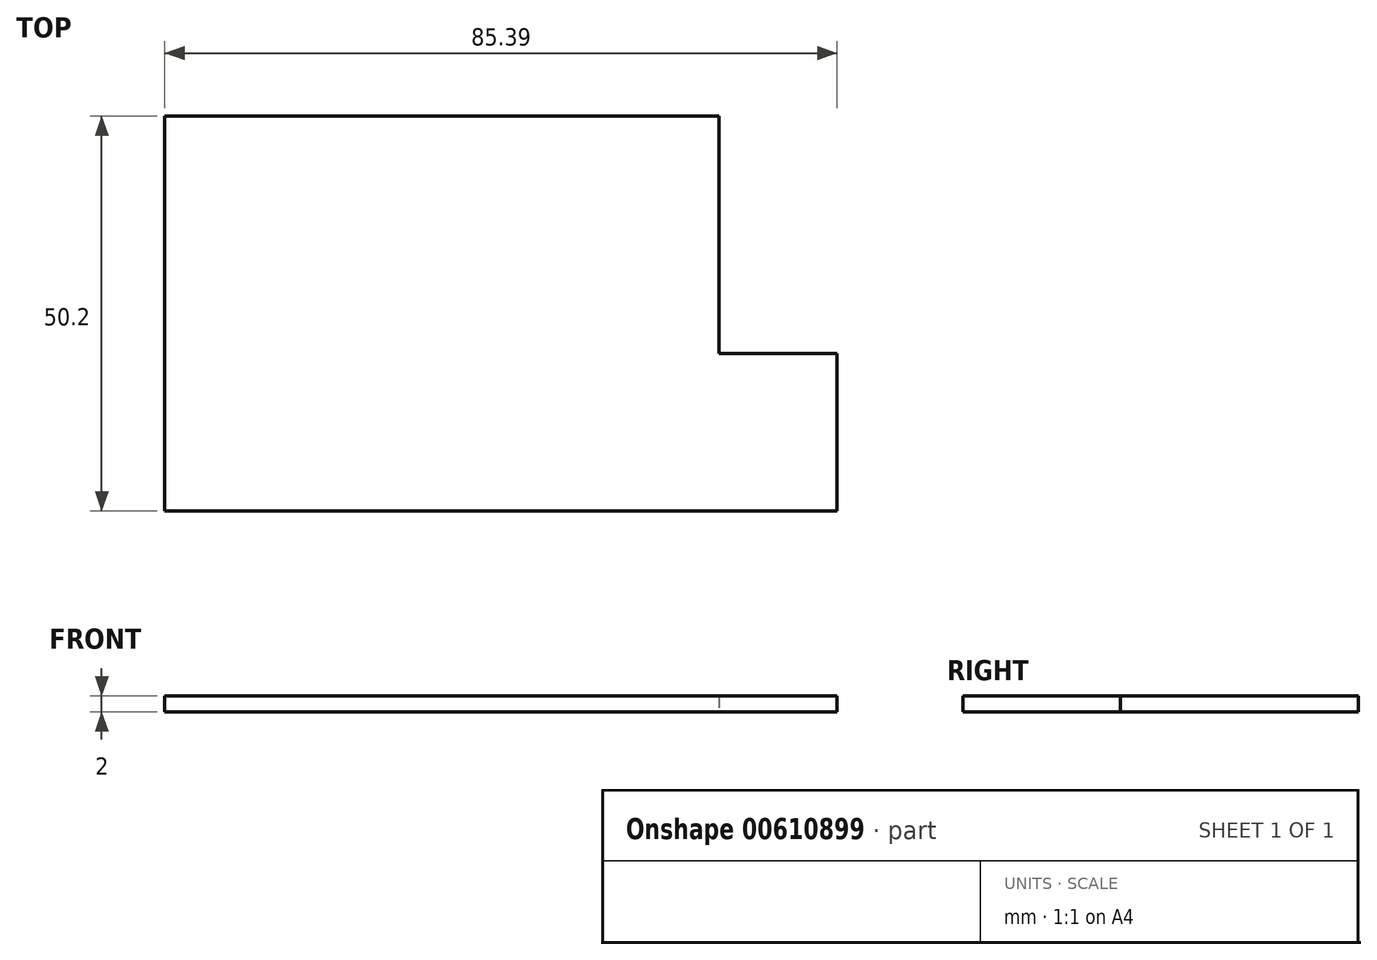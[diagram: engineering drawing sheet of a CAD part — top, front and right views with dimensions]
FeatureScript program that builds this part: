
annotation { "Feature Type Name" : "Feature", "Feature Type Description" : "" }
export const myFeature = defineFeature(function(context is Context, id is Id, definition is map)
    precondition{}
    {
        {
            var Q0;
            Q0=qCreatedBy(makeId("Top.planeOp"),FACE);
            var sketch = newSketch(context, id + "F0", { "sketchPlane" : qUnion([Q0])});
            skLineSegment(sketch, "E0.bottom", {"start": v(-62.02, 44.86) * mm, "end": v(8.37, 44.86) * mm});
            skLineSegment(sketch, "E0.top", {"start": v(-62.02, -5.34) * mm, "end": v(8.37, -5.34) * mm});
            skLineSegment(sketch, "E0.left", {"start": v(-62.02, 44.86) * mm, "end": v(-62.02, -5.34) * mm});
            skLineSegment(sketch, "E0.right", {"start": v(8.37, 44.86) * mm, "end": v(8.37, -5.34) * mm});
            skLineSegment(sketch, "E1.bottom", {"start": v(8.37, 14.66) * mm, "end": v(23.37, 14.66) * mm});
            skLineSegment(sketch, "E1.top", {"start": v(8.37, -5.34) * mm, "end": v(23.37, -5.34) * mm});
            skLineSegment(sketch, "E1.left", {"start": v(8.37, 14.66) * mm, "end": v(8.37, -5.34) * mm});
            skLineSegment(sketch, "E1.right", {"start": v(23.37, 14.66) * mm, "end": v(23.37, -5.34) * mm});
            skSolve(sketch);
        }
        {
            var Q0;
            Q0=makeQuery(id+"F0.imprint","IMPRINT",FACE,{"disambiguationData":[TD([[makeQuery(id+"F0.imprint","IMPRINT",EDGE,{"derivedFrom":sQuery(id+"F0.wireOp",EDGE,"E1.bottom")}),-1.0]])]});
            var Q1;
            Q1=makeQuery(id+"F0.imprint","IMPRINT",FACE,{"disambiguationData":[TD([[makeQuery(id+"F0.imprint","IMPRINT",EDGE,{"derivedFrom":sQuery(id+"F0.wireOp",EDGE,"E0.bottom")}),-1.0]])]});
            extrude(context, id + "F1", {"entities" : qUnion([Q0, Q1]), "depth" : 2 * mm, "offsetDistance" : 25 * mm});
        }
    });
